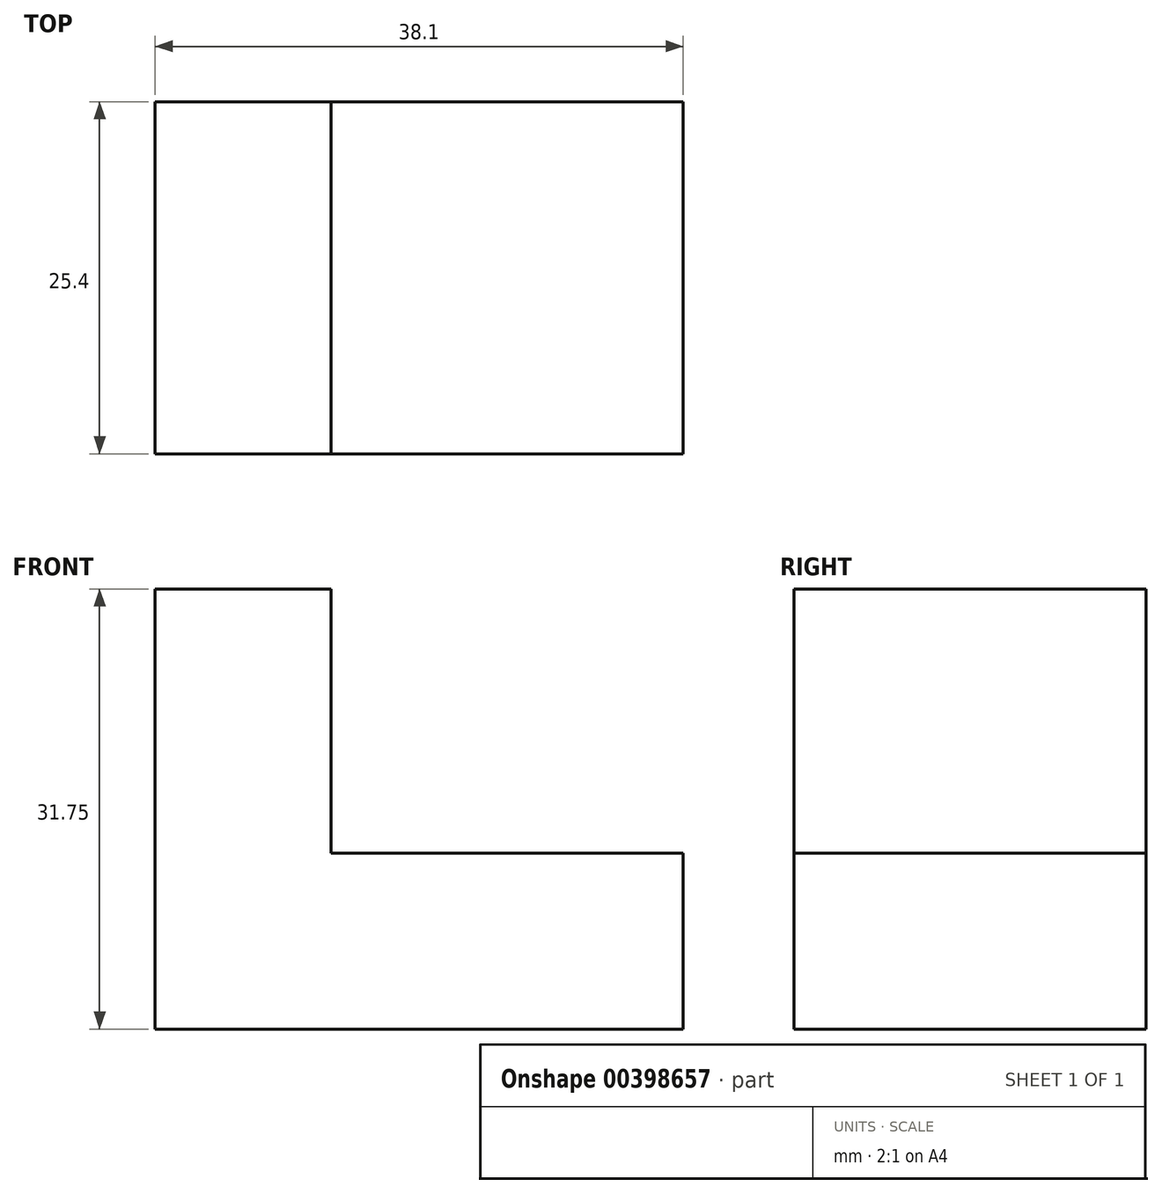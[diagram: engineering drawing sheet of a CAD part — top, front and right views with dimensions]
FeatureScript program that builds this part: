
annotation { "Feature Type Name" : "Feature", "Feature Type Description" : "" }
export const myFeature = defineFeature(function(context is Context, id is Id, definition is map)
    precondition{}
    {
        {
            var Q0;
            Q0=qCreatedBy(makeId("Front.planeOp"),FACE);
            var sketch = newSketch(context, id + "F0", { "sketchPlane" : qUnion([Q0])});
            skLineSegment(sketch, "E0", {"start": v(0, 0) * mm, "end": v(0, 31.75) * mm});
            skLineSegment(sketch, "E1", {"start": v(0, 31.75) * mm, "end": v(12.7, 31.75) * mm});
            skLineSegment(sketch, "E2", {"start": v(12.7, 31.75) * mm, "end": v(12.7, 12.7) * mm});
            skLineSegment(sketch, "E3", {"start": v(12.7, 12.7) * mm, "end": v(38.1, 12.7) * mm});
            skLineSegment(sketch, "E4", {"start": v(38.1, 12.7) * mm, "end": v(38.1, 0) * mm});
            skLineSegment(sketch, "E5", {"start": v(0, 0) * mm, "end": v(38.1, 0) * mm});
            skSolve(sketch);
        }
        {
            var Q0;
            Q0 = qSketchRegion(id + "F0", true);
            extrude(context, id + "F1", {"entities" : qUnion([Q0]), "depth" : 25.4 * mm});
        }
    });
